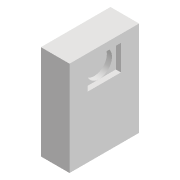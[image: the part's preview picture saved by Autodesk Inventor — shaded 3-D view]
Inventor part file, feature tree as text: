
AUTODESK INVENTOR PART (.ipt)
format: ipt  version: 2022 (Build 260153000, 153)  size: 111,616 bytes
history: native  units: mm
features: extrude x4, sketch x4, projected_geometry x3
ambient origin geometry x8: Origin, YZ Plane, XZ Plane, XY Plane, X Axis, Y Axis, Z Axis, Center Point
bodies: Volumenkörper1 (feature_tree)
feature tree (11):
  extrude  "Extrusion1"  Depth=13.6mm
  extrude  "Extrusion2"  Depth=6.5mm
  extrude  "Extrusion3"  Depth=1.5mm
  extrude  "Extrusion4"  Depth=1.0mm TaperAngle=0.0deg
  sketch  "Skizze1"  dims[d0=18.5mm d1=13.6mm]
  sketch  "Skizze2"  dims[d2=5.6mm d3=0.0mm d4=6.5mm]
  projected_geometry  "Projizierte Kontur1"
  sketch  "Skizze3"  dims[d5=5.0mm d6=1.5mm]
  projected_geometry  "Projizierte Kontur2"
  sketch  "Skizze4"  dims[d7=1.0mm d8=0.0mm d9=1.0mm d10=0.0mm d11=1.0mm d12=0.0mm]
  projected_geometry  "Projizierte Kontur3"
